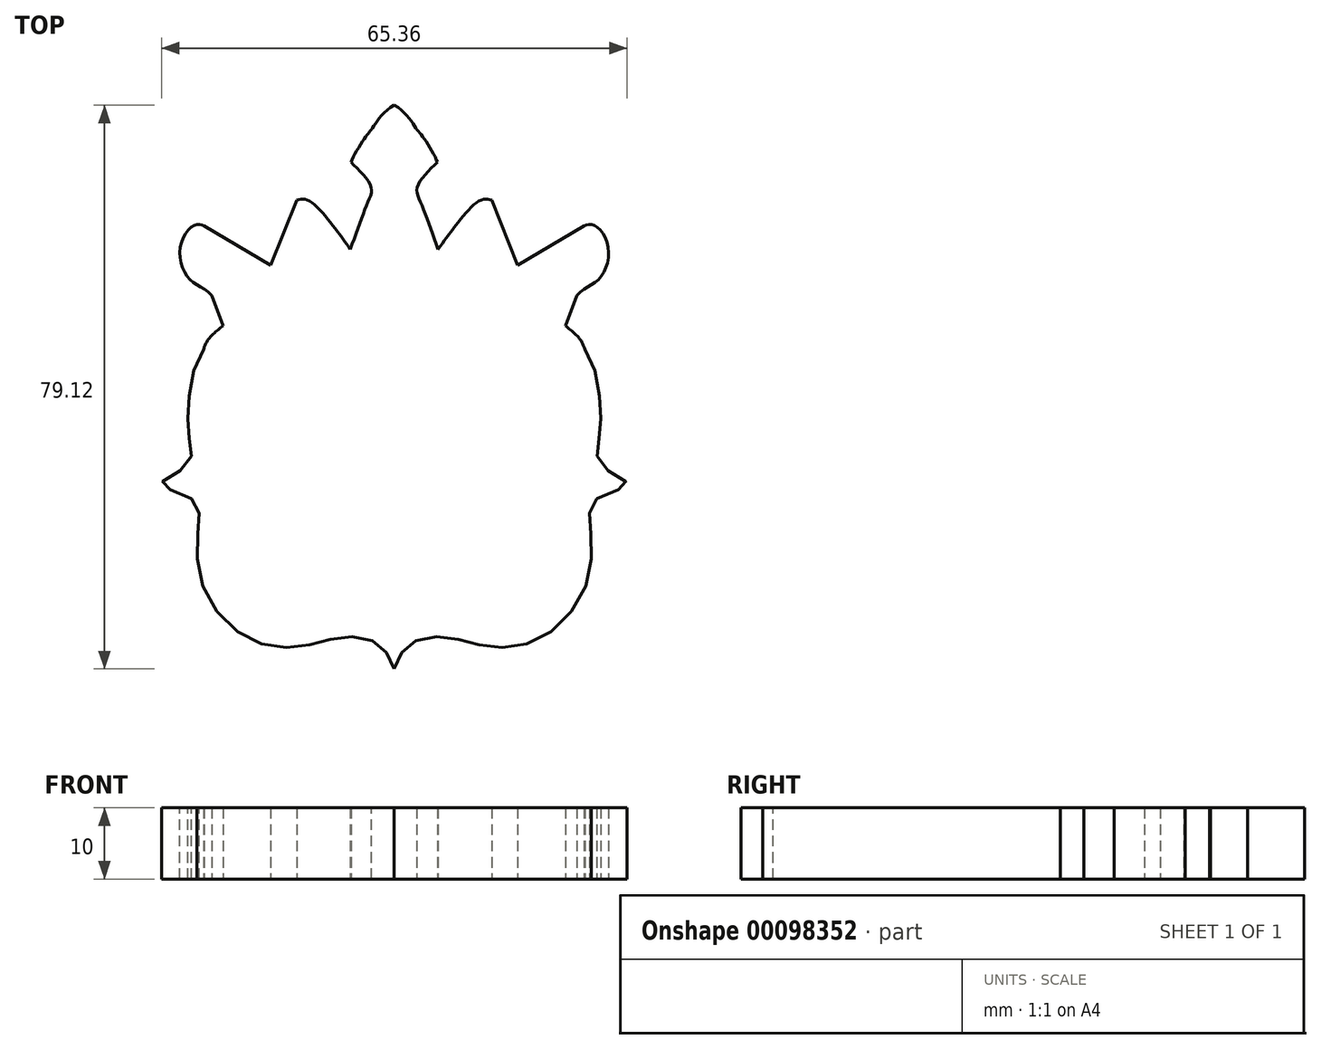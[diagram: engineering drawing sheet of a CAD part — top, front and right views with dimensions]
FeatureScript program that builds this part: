
annotation { "Feature Type Name" : "Feature", "Feature Type Description" : "" }
export const myFeature = defineFeature(function(context is Context, id is Id, definition is map)
    precondition{}
    {
        {
            var Q0;
            Q0=qCreatedBy(makeId("Top.planeOp"),FACE);
            var sketch = newSketch(context, id + "F0", { "sketchPlane" : qUnion([Q0])});
            skFitSpline(sketch, "E0", {"points": [v(0, -34.2) * mm, v(-2.15, -30.73) * mm, v(-7.37, -29.77) * mm, v(-13.22, -31.04) * mm, v(-20.81, -29.78) * mm, v(-27.14, -21.87) * mm, v(-27.46, -13.8) * mm, v(-28.4, -10.32) * mm, v(-32.68, -8.27) * mm, v(-29.04, -5.58) * mm, v(-28.72, -2.1) * mm, v(-28.88, 3.44) * mm, v(-26.78, 10.64) * mm, v(-24.03, 13.94) * mm, v(-25.72, 18.3) * mm, v(-28.88, 20.68) * mm, v(-29.99, 25.27) * mm, v(-27.93, 28.11) * mm, v(-26.67, 27.96) * mm], "startDerivative": vector(-28.92, 76.27) * mm, "endDerivative": vector(42.56, -17.3) * mm});
            skLineSegment(sketch, "E1", {"start": v(-26.67, 27.96) * mm, "end": v(-17.33, 22.42) * mm});
            skLineSegment(sketch, "E2", {"start": v(-17.33, 22.42) * mm, "end": v(-13.7, 31.6) * mm});
            skFitSpline(sketch, "E3", {"points": [v(-13.7, 31.6) * mm, v(-12.16, 31.6) * mm, v(-9, 28.5) * mm, v(-6.16, 24.68) * mm], "startDerivative": vector(6.5, 1.56) * mm, "endDerivative": vector(6.75, -9.39) * mm});
            skFitSpline(sketch, "E4", {"points": [v(-6.16, 24.68) * mm, v(-3.76, 31.12) * mm, v(-3.27, 33.5) * mm, v(-6.06, 36.91) * mm], "startDerivative": vector(6.12, 16.58) * mm, "endDerivative": vector(-9.37, 8.97) * mm});
            skFitSpline(sketch, "E5", {"points": [v(-6.06, 36.91) * mm, v(-4.12, 40.33) * mm, v(-3.03, 41.73) * mm, v(0, 44.91) * mm], "startDerivative": vector(2.72, 7.36) * mm, "endDerivative": vector(12.78, 7.27) * mm});
            skFitSpline(sketch, "E6", {"points": [v(0, -34.2) * mm, v(-2.15, -30.73) * mm, v(-7.37, -29.77) * mm, v(-13.22, -31.04) * mm, v(-20.81, -29.78) * mm, v(-27.14, -21.87) * mm, v(-27.46, -13.8) * mm, v(-28.4, -10.32) * mm, v(-32.68, -8.27) * mm, v(-29.04, -5.58) * mm, v(-28.72, -2.1) * mm, v(-28.88, 3.44) * mm, v(-26.78, 10.64) * mm, v(-24.03, 13.94) * mm, v(-25.72, 18.3) * mm, v(-28.88, 20.68) * mm, v(-29.99, 25.27) * mm, v(-27.93, 28.11) * mm, v(-26.67, 27.96) * mm], "startDerivative": vector(-28.92, 76.27) * mm, "endDerivative": vector(42.56, -17.3) * mm});
            skLineSegment(sketch, "E7", {"start": v(-25.62, 18.21) * mm, "end": v(-24.03, 13.94) * mm});
            skFitSpline(sketch, "E8", {"points": [v(-26.77, 10.65) * mm, v(-26.05, 12.1) * mm, v(-24.03, 13.94) * mm], "startDerivative": vector(1.24, 3.35) * mm, "endDerivative": vector(4.11, 3.22) * mm});
            skLineSegment(sketch, "E9", {"start": v(0, 44.91) * mm, "end": v(0, -34.2) * mm, "construction": true});
            skFitSpline(sketch, "E10.MirrorCS", {"points": [v(6.06, 36.91) * mm, v(4.12, 40.33) * mm, v(3.03, 41.73) * mm, v(0, 44.91) * mm], "startDerivative": vector(-2.72, 7.36) * mm, "endDerivative": vector(-12.78, 7.27) * mm});
            skFitSpline(sketch, "E11.MirrorCS", {"points": [v(6.16, 24.68) * mm, v(3.76, 31.12) * mm, v(3.27, 33.5) * mm, v(6.06, 36.91) * mm], "startDerivative": vector(-6.12, 16.58) * mm, "endDerivative": vector(9.37, 8.97) * mm});
            skFitSpline(sketch, "E12.MirrorCS", {"points": [v(13.7, 31.6) * mm, v(12.16, 31.6) * mm, v(9, 28.5) * mm, v(6.16, 24.68) * mm], "startDerivative": vector(-6.5, 1.56) * mm, "endDerivative": vector(-6.75, -9.39) * mm});
            skLineSegment(sketch, "E13.MirrorCS", {"start": v(17.33, 22.42) * mm, "end": v(13.7, 31.6) * mm});
            skLineSegment(sketch, "E14.MirrorCS", {"start": v(26.67, 27.96) * mm, "end": v(17.33, 22.42) * mm});
            skFitSpline(sketch, "E15.MirrorCS", {"points": [v(0, -34.2) * mm, v(2.15, -30.73) * mm, v(7.37, -29.77) * mm, v(13.22, -31.04) * mm, v(20.81, -29.78) * mm, v(27.14, -21.87) * mm, v(27.46, -13.8) * mm, v(28.4, -10.32) * mm, v(32.68, -8.27) * mm, v(29.04, -5.58) * mm, v(28.72, -2.1) * mm, v(28.88, 3.44) * mm, v(26.78, 10.64) * mm, v(24.03, 13.94) * mm, v(25.72, 18.3) * mm, v(28.88, 20.68) * mm, v(29.99, 25.27) * mm, v(27.93, 28.11) * mm, v(26.67, 27.96) * mm], "startDerivative": vector(28.92, 76.27) * mm, "endDerivative": vector(-42.56, -17.3) * mm});
            skFitSpline(sketch, "E16.MirrorCS", {"points": [v(0, -34.2) * mm, v(2.15, -30.73) * mm, v(7.37, -29.77) * mm, v(13.22, -31.04) * mm, v(20.81, -29.78) * mm, v(27.14, -21.87) * mm, v(27.46, -13.8) * mm, v(28.4, -10.32) * mm, v(32.68, -8.27) * mm, v(29.04, -5.58) * mm, v(28.72, -2.1) * mm, v(28.88, 3.44) * mm, v(26.78, 10.64) * mm, v(24.03, 13.94) * mm, v(25.72, 18.3) * mm, v(28.88, 20.68) * mm, v(29.99, 25.27) * mm, v(27.93, 28.11) * mm, v(26.67, 27.96) * mm], "startDerivative": vector(28.92, 76.27) * mm, "endDerivative": vector(-42.56, -17.3) * mm});
            skFitSpline(sketch, "E17.MirrorCS", {"points": [v(26.77, 10.65) * mm, v(26.05, 12.1) * mm, v(24.03, 13.94) * mm], "startDerivative": vector(-1.24, 3.35) * mm, "endDerivative": vector(-4.11, 3.22) * mm});
            skLineSegment(sketch, "E18.MirrorCS", {"start": v(25.62, 18.21) * mm, "end": v(24.03, 13.94) * mm});
            skSolve(sketch);
        }
        {
            var Q0;
            Q0 = qSketchRegion(id + "F0", true);
            extrude(context, id + "F1", {"entities" : qUnion([Q0]), "depth" : 10 * mm});
        }
    });
